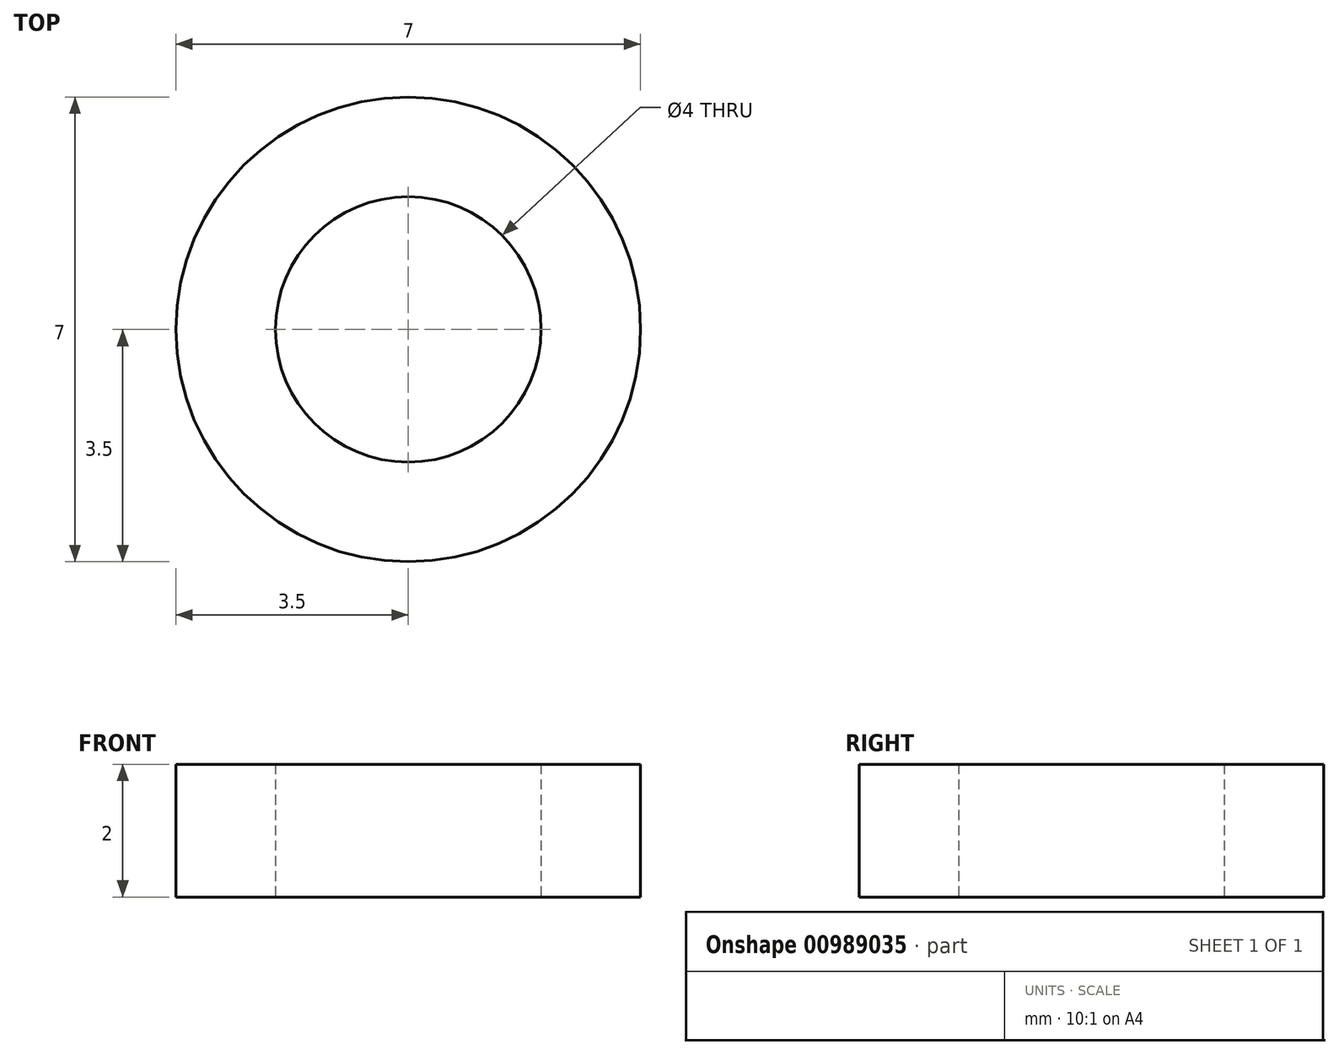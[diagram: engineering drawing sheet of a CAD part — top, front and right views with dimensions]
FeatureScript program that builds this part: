
annotation { "Feature Type Name" : "Feature", "Feature Type Description" : "" }
export const myFeature = defineFeature(function(context is Context, id is Id, definition is map)
    precondition{}
    {
        {
            var Q0;
            Q0=qCreatedBy(makeId("Top.planeOp"),FACE);
            var sketch = newSketch(context, id + "F0", { "sketchPlane" : qUnion([Q0])});
            skCircle(sketch, "E0", {"center": v(0, 0) * mm, "radius": 2 * mm});
            skCircle(sketch, "E1", {"center": v(0, 0) * mm, "radius": 3.5 * mm});
            skSolve(sketch);
        }
        {
            var Q0;
            Q0=makeQuery(id+"F0.imprint","IMPRINT",FACE,{"disambiguationData":[TD([[makeQuery(id+"F0.imprint","IMPRINT",EDGE,{"derivedFrom":sQuery(id+"F0.wireOp",EDGE,"E0")}),-1.0]])]});
            extrude(context, id + "F1", {"entities" : qUnion([Q0]), "depth" : 2 * mm, "offsetDistance" : 25 * mm});
        }
    });
